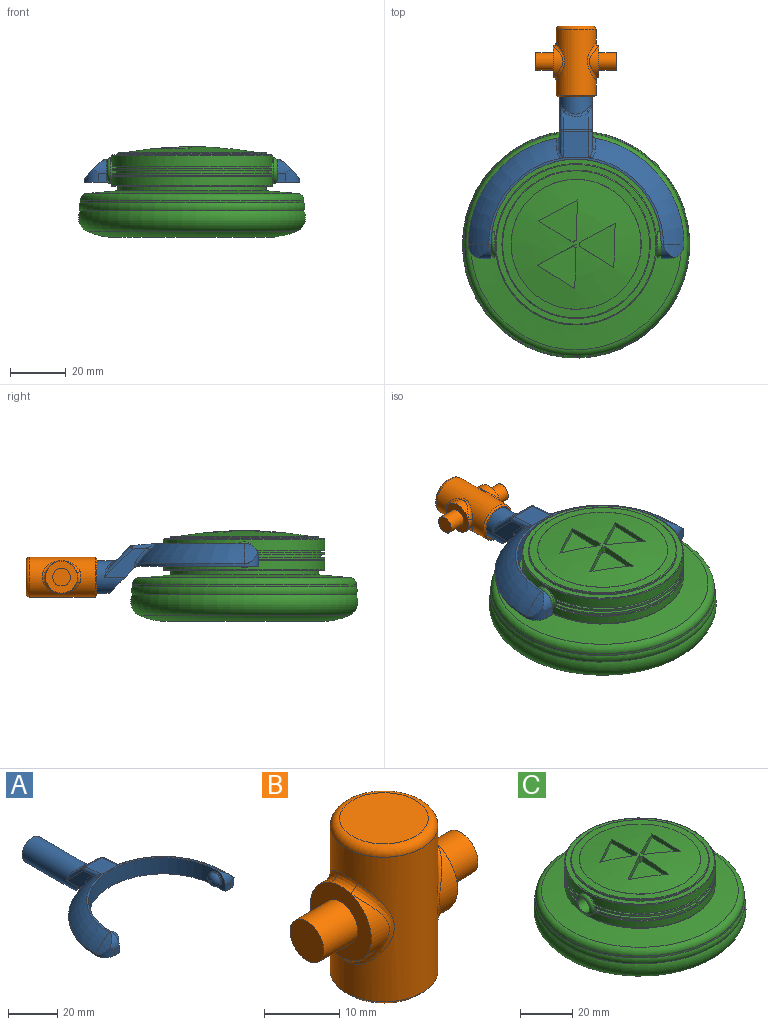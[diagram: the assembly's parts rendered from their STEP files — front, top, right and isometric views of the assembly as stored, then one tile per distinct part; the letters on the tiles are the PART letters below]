
ASSEMBLY  parts=3 mates=2
PART A: 48 faces, bbox 77.3x80.8x18.2 mm
  f0: plane 11.99x9.83mm, normal (0,-0.71,-0.71), area 141.5mm2, adj f1,f2,f9,f30,f43,f46
  f1: plane 15.39x10.49mm, normal (-1,0,0), area 63.5mm2, adj f0,f30,f32,f36,f46,f47
  f2: plane 15.39x10.49mm, normal (1,0,0), area 63.5mm2, adj f0,f30,f34,f39,f43,f44
  f3: plane 9.14x6.37mm, normal (0,0.71,0.71), area 67.6mm2, adj f35,f36,f39,f40
  f4: cylinder r=38.61mm len=37.99mm, axis (0,0,-1), area 42.6mm2, adj f6,f9,f17,f46,f47
  f5: torus R=19.3mm, axis (0,0,-1), area 507.8mm2, adj f10,f11,f12,f29,f42,f44
  f6: torus R=19.3mm, axis (0,0,-1), area 507.8mm2, adj f4,f11,f15,f28,f45,f47
  f7: cylinder r=30.48mm len=60.96mm, axis (0,0,-1), area 746.6mm2, adj f8,f9,f11,f14,f21,f24
  f8: plane 8.13x5.08mm, normal (-1,0,0), area 19.9mm2, adj f7,f9,f13,f19,f24
  f9: plane 77.22x43.73mm, normal (0,0,-1), area 956.2mm2, adj f0,f4,f7,f8,f10,f13,f14,f16
  f10: cylinder r=38.61mm len=37.99mm, axis (0,0,-1), area 42.6mm2, adj f5,f9,f20,f43,f44
  f11: plane 62.55x30.95mm, normal (0,0,1), area 75mm2, adj f5,f6,f7,f18,f19,f27
  f12: cylinder r=22.71mm len=7.33mm, axis (0,1,0), area 24.8mm2, adj f5,f19,f20
  f13: plane 3.05x3.05mm, normal (0,-1,0), area 9.3mm2, adj f8,f9,f19,f20
  f14: plane 8.13x5.08mm, normal (1,0,0), area 19.9mm2, adj f7,f9,f16,f18,f21
  f15: cylinder r=22.71mm len=7.33mm, axis (0,1,0), area 24.8mm2, adj f6,f17,f18
  f16: plane 3.05x3.05mm, normal (0,-1,0), area 9.3mm2, adj f9,f14,f17,f18
  f17: cylinder r=5.08mm len=5.08mm, axis (0,0,-1), area 21.9mm2, adj f4,f9,f15,f16,f18
  f18: cylinder r=5.08mm len=5.08mm, axis (-1,0,0), area 21.9mm2, adj f11,f14,f15,f16,f17
  f19: cylinder r=5.08mm len=5.08mm, axis (-1,0,0), area 21.9mm2, adj f8,f11,f12,f13,f20
  f20: cylinder r=5.08mm len=5.08mm, axis (0,0,-1), area 21.9mm2, adj f9,f10,f12,f13,f19
  f21: cylinder r=3.17mm len=6.35mm, axis (-1,0,0), area 12.7mm2, adj f7,f14,f23
  f22: plane 1.27x1.27mm, normal (1,0,0), area 1.3mm2, adj f23
  f23: torus R=0.64mm, axis (1,0,0), area 56.5mm2, adj f21,f22
  f24: cylinder r=3.17mm len=6.35mm, axis (1,0,0), area 12.7mm2, adj f7,f8,f26
  f25: plane 1.27x1.27mm, normal (-1,0,0), area 1.3mm2, adj f26
  f26: torus R=0.64mm, axis (-1,0,0), area 56.5mm2, adj f24,f25
  f27: plane 9.86x9.36mm, normal (0,0.09,1), area 85.6mm2, adj f11,f28,f29,f32,f34,f35,f42,f45
  f28: plane 1.04x0.17mm, normal (0,-1,0), area 0mm2, adj f6,f27,f45
  f29: plane 1.04x0.17mm, normal (0,-1,0), area 0mm2, adj f5,f27,f42
  f30: cylinder r=5.84mm len=33.01mm, axis (0,-1,0), area 1029.7mm2, adj f0,f1,f2,f31,f38,f40,f41
  f31: plane 11.68x11.68mm, normal (0,1,0), area 107.2mm2, adj f30
  f32: cylinder r=1.27mm len=9.13mm, axis (0,-1,0.09), area 14.4mm2, adj f1,f27,f33,f45
  f33: sphere r=1.27mm, area 1.5mm2, adj f32,f35,f36
  f34: cylinder r=1.27mm len=9.13mm, axis (0,1,-0.09), area 14.4mm2, adj f2,f27,f37,f42
  f35: cylinder r=1.27mm len=9.14mm, axis (-1,0,0), area 8.1mm2, adj f3,f27,f33,f37
  f36: cylinder r=1.27mm len=10.91mm, axis (0,-0.71,0.71), area 23.1mm2, adj f1,f3,f33,f38
  f37: sphere r=1.27mm, area 1.5mm2, adj f34,f35,f39
  f38: bspline ~4.55x2.75mm, area 2.3mm2, adj f30,f36,f40
  f39: cylinder r=1.27mm len=10.91mm, axis (0,0.71,-0.71), area 23.1mm2, adj f2,f3,f37,f41
  f40: bspline ~9.14x2.56mm, area 10.7mm2, adj f3,f30,f38,f41
  f41: bspline ~5.23x3.53mm, area 2.3mm2, adj f30,f39,f40
  f42: bspline ~4.62x3.14mm, area 5.2mm2, adj f5,f27,f29,f34,f44
  f43: cylinder r=1.27mm len=1.74mm, axis (0,0,-1), area 1.9mm2, adj f0,f2,f9,f10,f44
  f44: bspline ~8.6x7.86mm, area 11.9mm2, adj f2,f5,f10,f42,f43
  f45: bspline ~4.62x3.14mm, area 5.2mm2, adj f6,f27,f28,f32,f47
  f46: cylinder r=1.27mm len=1.74mm, axis (0,0,-1), area 1.9mm2, adj f0,f1,f4,f9,f47
  f47: bspline ~8.6x7.86mm, area 11.9mm2, adj f1,f4,f6,f45,f46
PART B: 25 faces, bbox 28.9x15.5x25.4 mm
  f0: cylinder r=5.71mm len=10.81mm, axis (-1,0,0), area 26.2mm2, adj f5,f15
  f1: cylinder r=5.71mm len=10.81mm, axis (-1,0,0), area 26.2mm2, adj f8,f11
  f2: cylinder r=7.14mm len=23.5mm, axis (0,0,-1), area 763.2mm2, adj f9,f10,f11,f12,f13,f14,f15,f16
  f3: plane 11.75x11.75mm, normal (0,0,1), area 108.4mm2, adj f17
  f4: plane 13.02x13.02mm, normal (0,0,-1), area 16.3mm2, adj f22,f24
  f5: plane 11.46x11.46mm, normal (1,0,0), area 70.9mm2, adj f0,f6,f13,f16,f18
  f6: cylinder r=5.71mm len=10.81mm, axis (-1,0,0), area 26.2mm2, adj f5,f14
  f7: cylinder r=5.71mm len=10.81mm, axis (-1,0,0), area 26.2mm2, adj f8,f10
  f8: plane 11.46x11.46mm, normal (-1,0,0), area 70.9mm2, adj f1,f7,f9,f12,f20
  f9: bspline ~4.64x1.73mm, area 6.5mm2, adj f2,f8,f10,f11
  f10: bspline ~13.62x4.91mm, area 20.7mm2, adj f2,f7,f9,f12
  f11: bspline ~13.6x4.87mm, area 20.7mm2, adj f1,f2,f9,f12
  f12: bspline ~4.64x1.73mm, area 6.5mm2, adj f2,f8,f10,f11
  f13: bspline ~4.64x1.73mm, area 6.5mm2, adj f2,f5,f14,f15
  f14: bspline ~13.62x4.91mm, area 20.7mm2, adj f2,f6,f13,f16
  f15: bspline ~13.6x4.87mm, area 20.7mm2, adj f0,f2,f13,f16
  f16: bspline ~4.64x1.73mm, area 6.5mm2, adj f2,f5,f14,f15
  f17: torus R=5.87mm, axis (0,0,1), area 83.8mm2, adj f2,f3
  f18: cylinder r=3.17mm len=6.35mm, axis (-1,0,0), area 126.7mm2, adj f5,f19
  f19: plane 6.35x6.35mm, normal (1,0,0), area 31.7mm2, adj f18
  f20: cylinder r=3.17mm len=6.35mm, axis (1,0,0), area 126.7mm2, adj f8,f21
  f21: plane 6.35x6.35mm, normal (-1,0,0), area 31.7mm2, adj f20
  f22: cylinder r=6.1mm len=22.86mm, axis (0,0,-1), area 875.6mm2, adj f4,f23
  f23: plane 12.19x12.19mm, normal (0,0,-1), area 116.7mm2, adj f22
  f24: cone r=7.14mm half-angle=45deg, axis (0,0,1), area 38.5mm2, adj f2,f4
PART C: 64 faces, bbox 96.3x96.3x32.5 mm
  f0: cylinder r=28.87mm len=57.73mm, axis (0,0,-1), area 585.4mm2, adj f1,f2,f54,f55,f60
  f1: plane 57.17x24.83mm, normal (0,0,1), area 102.6mm2, adj f0,f3,f54,f55
  f2: plane 57.17x24.83mm, normal (0,0,1), area 102.7mm2, adj f0,f4,f54,f55
  f3: cylinder r=27.59mm len=54.59mm, axis (0,0,-1), area 33.2mm2, adj f1,f6,f54,f55
  f4: cylinder r=27.59mm len=54.59mm, axis (0,0,-1), area 33.2mm2, adj f2,f5,f54,f55
  f5: plane 57.22x24.69mm, normal (0,0,-1), area 102.1mm2, adj f4,f8,f54,f55
  f6: plane 57.22x24.69mm, normal (0,0,-1), area 102.1mm2, adj f3,f7,f54,f55
  f7: cylinder r=28.87mm len=57.11mm, axis (0,0,-1), area 67.6mm2, adj f6,f9,f54,f55
  f8: cylinder r=28.87mm len=57.11mm, axis (0,0,-1), area 67.6mm2, adj f5,f10,f54,f55
  f9: plane 57.04x24.39mm, normal (0,0,1), area 101.2mm2, adj f7,f11,f54,f55
  f10: plane 57.04x24.39mm, normal (0,0,1), area 101.2mm2, adj f8,f12,f54,f55
  f11: cylinder r=27.6mm len=54.46mm, axis (0,0,-1), area 69mm2, adj f9,f14,f54,f55
  f12: cylinder r=27.6mm len=54.46mm, axis (0,0,-1), area 69mm2, adj f10,f13,f54,f55
  f13: plane 57.12x24.35mm, normal (0,0,-1), area 100.9mm2, adj f12,f16,f54,f55
  f14: plane 57.12x24.35mm, normal (0,0,-1), area 101mm2, adj f11,f15,f54,f55
  f15: cylinder r=28.87mm len=57.03mm, axis (0,0,-1), area 67.3mm2, adj f14,f17,f54,f55
  f16: cylinder r=28.87mm len=57.03mm, axis (0,0,-1), area 67.3mm2, adj f13,f18,f54,f55
  f17: plane 57.04x24.38mm, normal (0,0,1), area 101.2mm2, adj f15,f19,f54,f55
  f18: plane 57.04x24.38mm, normal (0,0,1), area 101.2mm2, adj f16,f20,f54,f55
  f19: cylinder r=27.6mm len=54.51mm, axis (0,0,-1), area 49.4mm2, adj f17,f22,f54,f55
  f20: cylinder r=27.6mm len=54.51mm, axis (0,0,-1), area 49.4mm2, adj f18,f21,f54,f55
  f21: plane 57.19x24.59mm, normal (0,0,-1), area 101.6mm2, adj f20,f23,f54,f55
  f22: plane 57.19x24.59mm, normal (0,0,-1), area 101.6mm2, adj f19,f23,f54,f55
  f23: cylinder r=28.87mm len=57.73mm, axis (0,0,-1), area 668.8mm2, adj f21,f22,f54,f55,f61
  f24: sphere r=135.39mm, area 1385.3mm2, adj f38,f39,f40,f41,f43,f44,f45,f46
  f25: plane 39.33x39.33mm, normal (0,0,-1), area 1214.6mm2, adj f26
  f26: torus R=20.12mm, axis (0,0,-1), area 1429.3mm2, adj f25,f27
  f27: torus R=27.74mm, axis (0,0,-1), area 3542.1mm2, adj f26,f28
  f28: torus R=35.36mm, axis (0,0,-1), area 2180.1mm2, adj f27,f29
  f29: torus R=37.35mm, axis (0,0,-1), area 734.6mm2, adj f28,f30
  f30: cylinder r=40.06mm len=80.11mm, axis (0,0,-1), area 213.3mm2, adj f29,f34
  f31: cone r=26.57mm half-angle=85deg, axis (0,0,-1), area 2265mm2, adj f32,f34
  f32: cylinder r=26.57mm len=53.14mm, axis (0,0,-1), area 265mm2, adj f31,f33
  f33: plane 57.23x57.23mm, normal (0,0,-1), area 354.5mm2, adj f32,f60
  f34: torus R=37.52mm, axis (0,0,1), area 928.6mm2, adj f30,f31
  f35: cone r=26.57mm half-angle=87deg, axis (0,0,-1), area 475.4mm2, adj f62,f63
  f36: cylinder r=26.57mm len=53.14mm, axis (0,0,-1), area 92.3mm2, adj f37,f62
  f37: plane 57.23x57.23mm, normal (0,0,1), area 354.5mm2, adj f36,f61
  f38: cylinder r=1.27mm len=2.53mm, axis (0,0,1), area 3.4mm2, adj f24,f39,f41,f42
  f39: plane 14.6x2.53mm, normal (-1,0.03,0), area 32.2mm2, adj f24,f38,f40,f42
  f40: plane 13.98x7.52mm, normal (0.47,-0.88,0), area 28mm2, adj f24,f39,f41,f42
  f41: plane 12.42x7.68mm, normal (0.53,0.85,0), area 32.2mm2, adj f24,f38,f40,f42
  f42: plane 15.2x13.98mm, normal (0,0,1), area 108.3mm2, adj f38,f39,f40,f41
  f43: plane 12.86x6.92mm, normal (0.47,-0.88,0), area 32.2mm2, adj f24,f44,f46,f47
  f44: cylinder r=1.27mm len=2.53mm, axis (0,0,1), area 3.4mm2, adj f24,f43,f45,f47
  f45: plane 12.42x7.68mm, normal (0.53,0.85,0), area 32.2mm2, adj f24,f44,f46,f47
  f46: plane 15.87x1.84mm, normal (-1,0.03,0), area 28mm2, adj f24,f43,f45,f47
  f47: plane 15.87x12.9mm, normal (0,0,1), area 108.3mm2, adj f43,f44,f45,f46
  f48: cylinder r=1.27mm len=2.53mm, axis (0,0,1), area 3.4mm2, adj f24,f49,f51,f52
  f49: plane 12.86x6.92mm, normal (0.47,-0.88,0), area 32.2mm2, adj f24,f48,f50,f52
  f50: plane 13.5x8.35mm, normal (0.53,0.85,0), area 28mm2, adj f24,f49,f51,f52
  f51: plane 14.6x2.53mm, normal (-1,0.03,0), area 32.2mm2, adj f24,f48,f50,f52
  f52: plane 15.27x13.94mm, normal (0,0,1), area 108.3mm2, adj f48,f49,f50,f51
  f53: plane 6.6x6.6mm, normal (1,0,0), area 2.6mm2, adj f58,f59
  f54: cylinder r=4.57mm len=9.14mm, axis (-1,0,0), area 20.3mm2, adj f0,f1,f2,f3,f4,f5,f6,f7
  f55: cylinder r=4.57mm len=9.14mm, axis (-1,0,0), area 22.3mm2, adj f0,f1,f2,f3,f4,f5,f6,f7
  f56: plane 6.6x6.6mm, normal (-1,0,0), area 2.6mm2, adj f57,f59
  f57: torus R=3.3mm, axis (1,0,0), area 51.5mm2, adj f55,f56
  f58: torus R=3.3mm, axis (1,0,0), area 51.5mm2, adj f53,f54
  f59: cylinder r=3.17mm len=60.96mm, axis (1,0,0), area 1216.1mm2, adj f53,f56
  f60: torus R=28.61mm, axis (0,0,1), area 72.1mm2, adj f0,f33
  f61: torus R=28.61mm, axis (0,0,-1), area 72.1mm2, adj f23,f37
  f62: torus R=26.31mm, axis (0,0,1), area 64.2mm2, adj f35,f36
  f63: torus R=23.29mm, axis (0,0,1), area 4.5mm2, adj f24,f35
PLACE A t=(32.34,27.52,20.85)mm
PLACE B rot(axis=(-1,0,0),90deg) t=(32.34,80.3,16.88)mm
PLACE C t=(32.34,27.52,33.52)mm
MATE revolute A.f24 <-> C.f54  axis (-1,0,0) through (62.82,27.52,24.92)mm
MATE revolute B.f2 <-> A.f30  axis (0,-1,0) through (32.34,103.16,16.88)mm
